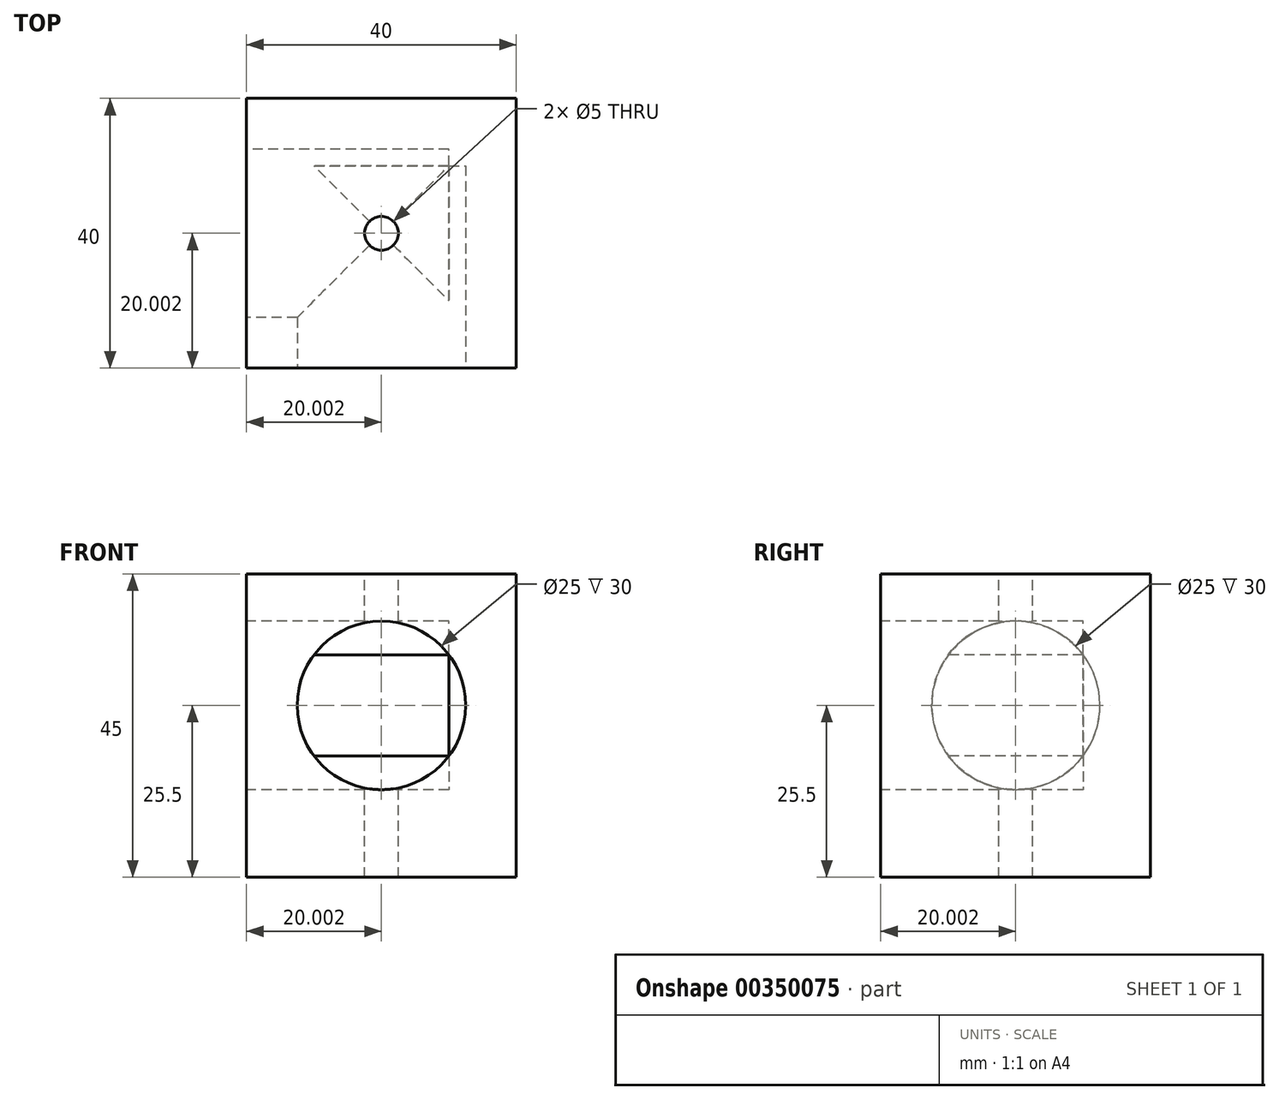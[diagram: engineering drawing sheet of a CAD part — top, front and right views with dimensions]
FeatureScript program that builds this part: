
annotation { "Feature Type Name" : "Feature", "Feature Type Description" : "" }
export const myFeature = defineFeature(function(context is Context, id is Id, definition is map)
    precondition{}
    {
        {
            var Q0;
            Q0=qCreatedBy(makeId("Top.planeOp"),FACE);
            var sketch = newSketch(context, id + "F0", { "sketchPlane" : qUnion([Q0])});
            skLineSegment(sketch, "E0.bottom", {"start": v(-18.6, 13.82) * mm, "end": v(21.4, 13.82) * mm});
            skLineSegment(sketch, "E0.top", {"start": v(-18.6, -26.18) * mm, "end": v(21.4, -26.18) * mm});
            skLineSegment(sketch, "E0.left", {"start": v(-18.6, 13.82) * mm, "end": v(-18.6, -26.18) * mm});
            skLineSegment(sketch, "E0.right", {"start": v(21.4, 13.82) * mm, "end": v(21.4, -26.18) * mm});
            skSolve(sketch);
        }
        {
            var Q0;
            Q0=makeQuery(id+"F0.imprint","IMPRINT",FACE,{"disambiguationData":[TD([[makeQuery(id+"F0.imprint","IMPRINT",EDGE,{"derivedFrom":sQuery(id+"F0.wireOp",EDGE,"E0.bottom")}),-1.0]])]});
            extrude(context, id + "F1", {"entities" : qUnion([Q0]), "depth" : 45 * mm});
        }
        {
            var Q0;
            Q0=makeQuery(id+"F1.opExtrude","SWEPT_FACE",FACE,{"disambiguationData":[OSD([sQuery(id+"F0.wireOp",EDGE,"E0.left")])]});
            var sketch = newSketch(context, id + "F2", { "sketchPlane" : qUnion([Q0])});
            skCircle(sketch, "E1", {"center": v(6.18, 25.5) * mm, "radius": 12.5 * mm});
            skPoint(sketch, "E1.centerSnap0", {"position": v(6.18, 0) * mm});
            skSolve(sketch);
        }
        {
            var Q0;
            Q0=makeQuery(id+"F1.opExtrude","SWEPT_FACE",FACE,{"disambiguationData":[OSD([sQuery(id+"F0.wireOp",EDGE,"E0.top")])]});
            var sketch = newSketch(context, id + "F3", { "sketchPlane" : qUnion([Q0])});
            skCircle(sketch, "E2", {"center": v(1.4, 25.5) * mm, "radius": 12.5 * mm});
            skPoint(sketch, "E2.centerSnap0", {"position": v(1.4, 0) * mm});
            skSolve(sketch);
        }
        {
            var Q0;
            Q0=makeQuery(id+"F3.imprint","IMPRINT",FACE,{"disambiguationData":[TD([[makeQuery(id+"F3.imprint","IMPRINT",EDGE,{"derivedFrom":sQuery(id+"F3.wireOp",EDGE,"E2")}),1.0]])]});
            extrude(context, id + "F4", {"entities" : qUnion([Q0]), "operationType" : NewBodyOperationType.REMOVE, "oppositeDirection" : true, "depth" : 30 * mm});
        }
        {
            var Q0;
            Q0=makeQuery(id+"F2.imprint","IMPRINT",FACE,{"disambiguationData":[TD([[makeQuery(id+"F2.imprint","IMPRINT",EDGE,{"derivedFrom":sQuery(id+"F2.wireOp",EDGE,"E1")}),1.0]])]});
            extrude(context, id + "F5", {"entities" : qUnion([Q0]), "operationType" : NewBodyOperationType.REMOVE, "oppositeDirection" : true, "depth" : 30 * mm});
        }
        {
            var Q0;
            Q0=makeQuery(id+"F1.opExtrude","CAP_FACE",FACE,{"disambiguationData":[OSD([sQuery(id+"F0.wireOp",EDGE,"E0.bottom"),sQuery(id+"F0.wireOp",EDGE,"E0.top"),sQuery(id+"F0.wireOp",EDGE,"E0.left"),sQuery(id+"F0.wireOp",EDGE,"E0.right")])],"isStart":false});
            var sketch = newSketch(context, id + "F6", { "sketchPlane" : qUnion([Q0])});
            skCircle(sketch, "E3", {"center": v(1.4, -6.18) * mm, "radius": 2.5 * mm});
            skPoint(sketch, "E3.centerSnap0", {"position": v(-18.6, -6.18) * mm});
            skPoint(sketch, "E3.centerSnap1", {"position": v(1.4, -26.18) * mm});
            skSolve(sketch);
        }
        {
            var Q0;
            Q0=makeQuery(id+"F6.imprint","IMPRINT",FACE,{"disambiguationData":[TD([[makeQuery(id+"F6.imprint","IMPRINT",EDGE,{"derivedFrom":sQuery(id+"F6.wireOp",EDGE,"E3")}),1.0]])]});
            extrude(context, id + "F7", {"entities" : qUnion([Q0]), "operationType" : NewBodyOperationType.REMOVE, "endBound" : BoundingType.THROUGH_ALL, "oppositeDirection" : true, "depth" : 25 * mm});
        }
    });
